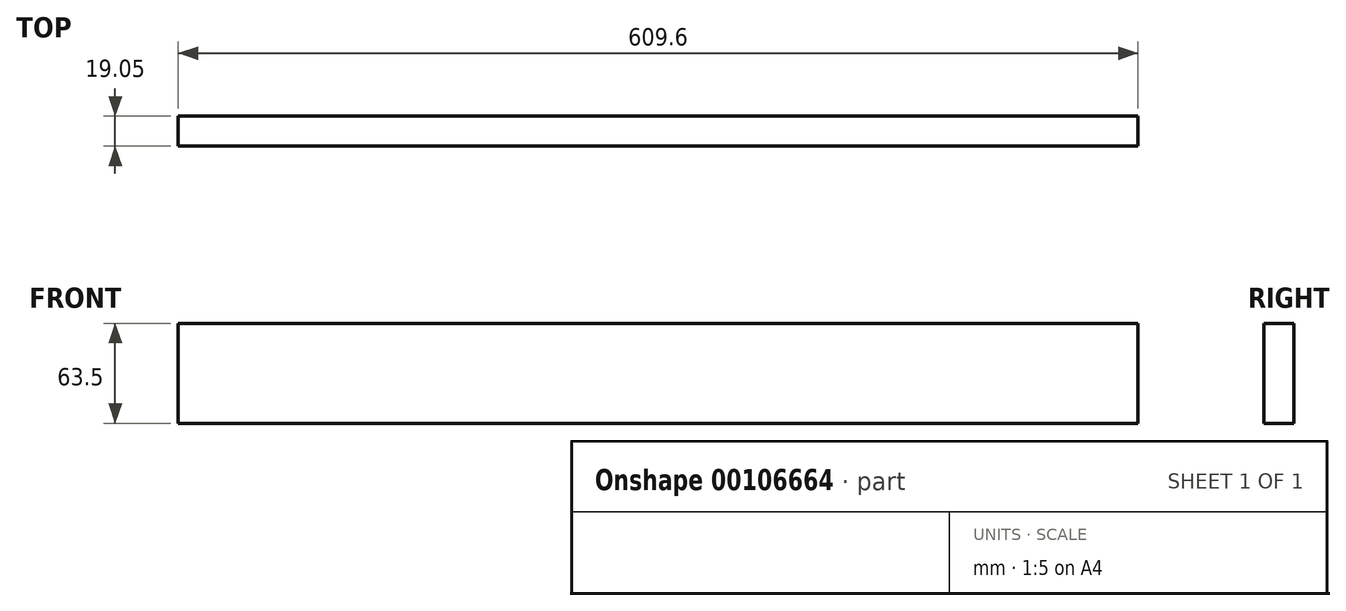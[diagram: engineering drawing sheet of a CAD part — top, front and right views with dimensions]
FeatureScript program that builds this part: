
annotation { "Feature Type Name" : "Feature", "Feature Type Description" : "" }
export const myFeature = defineFeature(function(context is Context, id is Id, definition is map)
    precondition{}
    {
        {
            var Q0;
            Q0=qCreatedBy(makeId("Front.planeOp"),FACE);
            var sketch = newSketch(context, id + "F0", { "sketchPlane" : qUnion([Q0])});
            skLineSegment(sketch, "E0.bottom", {"start": v(0, 0) * mm, "end": v(609.6, 0) * mm});
            skLineSegment(sketch, "E0.top", {"start": v(0, 63.5) * mm, "end": v(609.6, 63.5) * mm});
            skLineSegment(sketch, "E0.left", {"start": v(0, 0) * mm, "end": v(0, 63.5) * mm});
            skLineSegment(sketch, "E0.right", {"start": v(609.6, 0) * mm, "end": v(609.6, 63.5) * mm});
            skSolve(sketch);
        }
        {
            var Q0;
            Q0=makeQuery(id+"F0.imprint","IMPRINT",FACE,{"disambiguationData":[TD([[makeQuery(id+"F0.imprint","IMPRINT",EDGE,{"derivedFrom":sQuery(id+"F0.wireOp",EDGE,"E0.bottom")}),1.0]])]});
            extrude(context, id + "F1", {"entities" : qUnion([Q0]), "depth" : 19.05 * mm});
        }
    });
